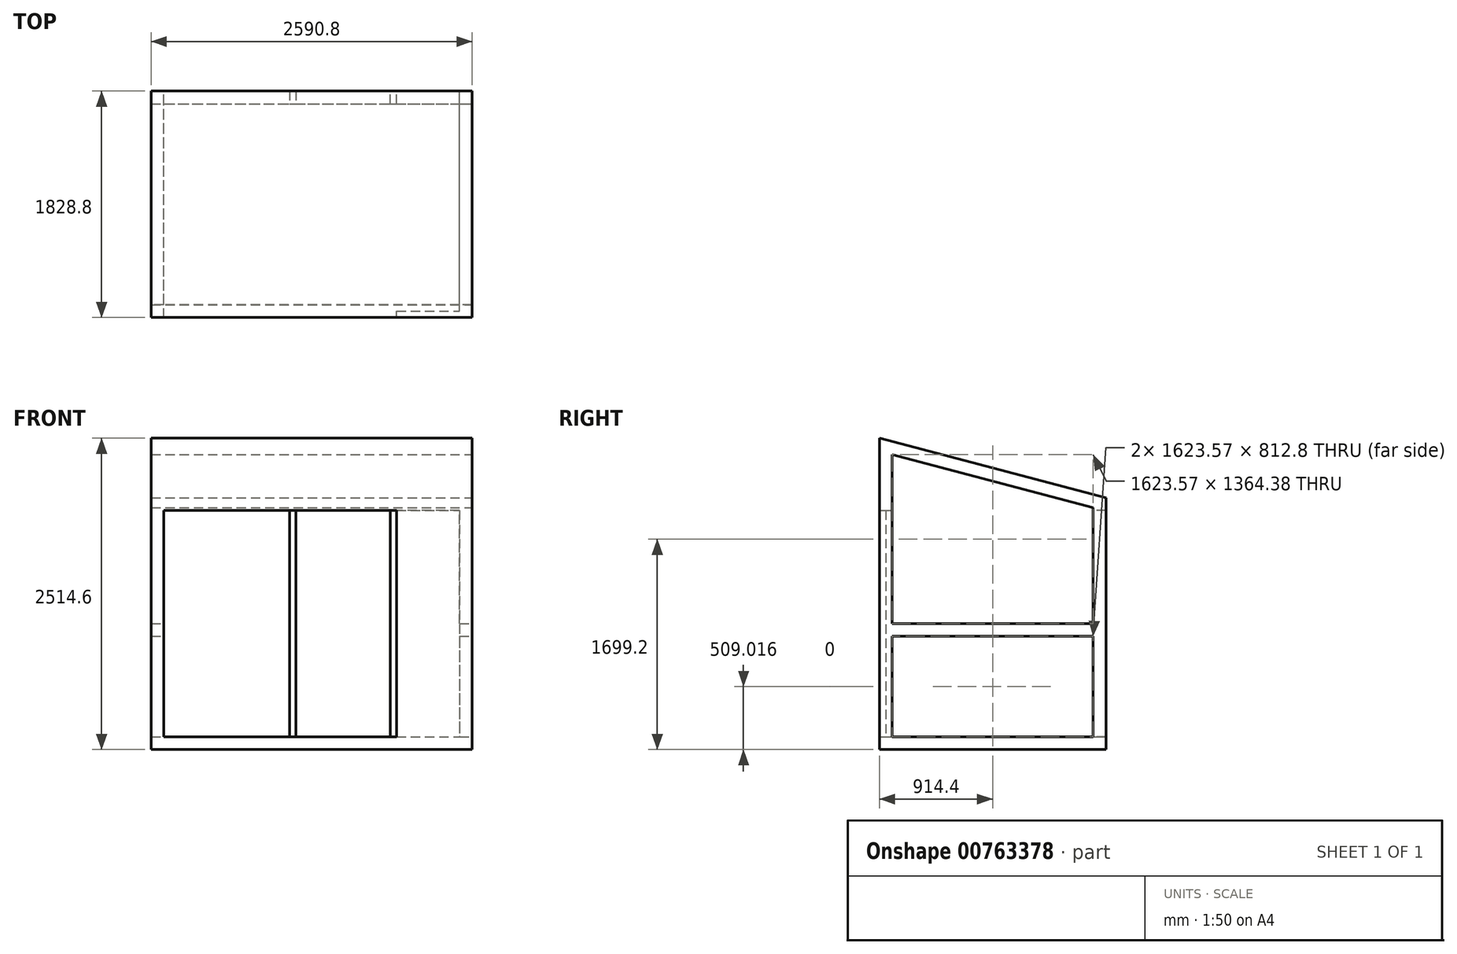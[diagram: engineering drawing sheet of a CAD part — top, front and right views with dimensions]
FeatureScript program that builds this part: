
annotation { "Feature Type Name" : "Feature", "Feature Type Description" : "" }
export const myFeature = defineFeature(function(context is Context, id is Id, definition is map)
    precondition{}
    {
        {
            var Q0;
            Q0=qCreatedBy(makeId("Top.planeOp"),FACE);
            var sketch = newSketch(context, id + "F0", { "sketchPlane" : qUnion([Q0])});
            skLineSegment(sketch, "E0.bottom", {"start": v(-1295.4, 914.4) * mm, "end": v(1295.4, 914.4) * mm});
            skLineSegment(sketch, "E0.top", {"start": v(-1295.4, -914.4) * mm, "end": v(1295.4, -914.4) * mm});
            skLineSegment(sketch, "E0.left", {"start": v(-1295.4, 914.4) * mm, "end": v(-1295.4, -914.4) * mm});
            skLineSegment(sketch, "E0.right", {"start": v(1295.4, 914.4) * mm, "end": v(1295.4, -914.4) * mm});
            skPoint(sketch, "E0.middle", {"position": v(0, 0) * mm});
            skSolve(sketch);
        }
        {
            var Q0;
            Q0=makeQuery(id+"F0.imprint","IMPRINT",FACE,{"disambiguationData":[TD([[makeQuery(id+"F0.imprint","IMPRINT",EDGE,{"derivedFrom":sQuery(id+"F0.wireOp",EDGE,"E0.bottom")}),-1.0]])]});
            extrude(context, id + "F1", {"entities" : qUnion([Q0]), "depth" : 2514.6 * mm, "offsetDistance" : 25.4 * mm});
        }
        {
            var Q0;
            Q0=makeQuery(id+"F1.opExtrude","SWEPT_FACE",FACE,{"disambiguationData":[OSD([sQuery(id+"F0.wireOp",EDGE,"E0.right")])]});
            var sketch = newSketch(context, id + "F2", { "sketchPlane" : qUnion([Q0])});
            skLineSegment(sketch, "E1", {"start": v(-914.4, 2514.6) * mm, "end": v(914.4, 2032) * mm});
            skLineSegment(sketch, "E2", {"start": v(914.4, 2032) * mm, "end": v(914.4, 2514.6) * mm});
            skLineSegment(sketch, "E3", {"start": v(914.4, 2514.6) * mm, "end": v(-914.4, 2514.6) * mm});
            skSolve(sketch);
        }
        {
            var Q0;
            Q0=makeQuery(id+"F2.imprint","IMPRINT",FACE,{"disambiguationData":[TD([[makeQuery(id+"F2.imprint","IMPRINT",EDGE,{"derivedFrom":sQuery(id+"F2.wireOp",EDGE,"E1")}),1.0]])]});
            extrude(context, id + "F3", {"entities" : qUnion([Q0]), "operationType" : NewBodyOperationType.REMOVE, "endBound" : BoundingType.THROUGH_ALL, "oppositeDirection" : true, "depth" : 25.4 * mm, "offsetDistance" : 25.4 * mm});
        }
        {
            var Q0;
            Q0=makeQuery(id+"F1.opExtrude","SWEPT_FACE",FACE,{"disambiguationData":[OSD([sQuery(id+"F0.wireOp",EDGE,"E0.right")])]});
            var sketch = newSketch(context, id + "F4", { "sketchPlane" : qUnion([Q0])});
            skLineSegment(sketch, "E4.0", {"start": v(811.78, 1952.95) * mm, "end": v(-811.78, 2381.4) * mm});
            skLineSegment(sketch, "E4.1", {"start": v(811.78, 102.62) * mm, "end": v(811.78, 1952.95) * mm});
            skLineSegment(sketch, "E4.2", {"start": v(-811.78, 102.62) * mm, "end": v(811.78, 102.62) * mm});
            skLineSegment(sketch, "E4.3", {"start": v(-811.78, 2381.4) * mm, "end": v(-811.78, 102.62) * mm});
            skLineSegment(sketch, "E5.0", {"start": v(812.8, 1953.73) * mm, "end": v(-812.8, 2382.71) * mm});
            skLineSegment(sketch, "E5.1", {"start": v(812.8, 101.6) * mm, "end": v(812.8, 1953.73) * mm});
            skLineSegment(sketch, "E5.2", {"start": v(-812.8, 101.6) * mm, "end": v(812.8, 101.6) * mm});
            skLineSegment(sketch, "E5.3", {"start": v(-812.8, 2382.71) * mm, "end": v(-812.8, 101.6) * mm});
            skSolve(sketch);
        }
        {
            var Q0;
            Q0=makeQuery(id+"F4.imprint","IMPRINT",FACE,{"disambiguationData":[TD([[makeQuery(id+"F4.imprint","IMPRINT",EDGE,{"derivedFrom":sQuery(id+"F4.wireOp",EDGE,"E4.0")}),1.0]])]});
            extrude(context, id + "F5", {"entities" : qUnion([Q0]), "operationType" : NewBodyOperationType.REMOVE, "endBound" : BoundingType.THROUGH_ALL, "oppositeDirection" : true, "depth" : 25.4 * mm, "offsetDistance" : 25.4 * mm});
        }
        {
            var Q0;
            Q0=makeQuery(id+"F1.opExtrude","SWEPT_FACE",FACE,{"disambiguationData":[OSD([sQuery(id+"F0.wireOp",EDGE,"E0.bottom")])]});
            var sketch = newSketch(context, id + "F6", { "sketchPlane" : qUnion([Q0])});
            skLineSegment(sketch, "E6.0", {"start": v(1193.8, 101.6) * mm, "end": v(1193.8, 1930.4) * mm});
            skLineSegment(sketch, "E6.1", {"start": v(-1193.8, 101.6) * mm, "end": v(1193.8, 101.6) * mm});
            skLineSegment(sketch, "E6.2", {"start": v(-1193.8, 1930.4) * mm, "end": v(-1193.8, 101.6) * mm});
            skLineSegment(sketch, "E6.3", {"start": v(1193.8, 1930.4) * mm, "end": v(-1193.8, 1930.4) * mm});
            skSolve(sketch);
        }
        {
            var Q0;
            Q0=makeQuery(id+"F6.imprint","IMPRINT",FACE,{"disambiguationData":[TD([[makeQuery(id+"F6.imprint","IMPRINT",EDGE,{"derivedFrom":sQuery(id+"F6.wireOp",EDGE,"E6.0")}),1.0]])]});
            extrude(context, id + "F7", {"entities" : qUnion([Q0]), "operationType" : NewBodyOperationType.REMOVE, "endBound" : BoundingType.THROUGH_ALL, "oppositeDirection" : true, "depth" : 127 * mm, "offsetDistance" : 25.4 * mm});
        }
        {
            var Q0;
            Q0=makeQuery(id+"F5.boolean.opBoolean","COPY",FACE,{"derivedFrom":makeQuery(id+"F5.opExtrude","SWEPT_FACE",FACE,{"disambiguationData":[OSD([sQuery(id+"F4.wireOp",EDGE,"E4.1")])]})});
            var sketch = newSketch(context, id + "F8", { "sketchPlane" : qUnion([Q0])});
            skLineSegment(sketch, "E7.bottom", {"start": v(-1295.4, 1017.02) * mm, "end": v(-1193.8, 1017.02) * mm});
            skLineSegment(sketch, "E7.top", {"start": v(-1295.4, 915.42) * mm, "end": v(-1193.8, 915.42) * mm});
            skLineSegment(sketch, "E7.left", {"start": v(-1295.4, 1017.02) * mm, "end": v(-1295.4, 915.42) * mm});
            skLineSegment(sketch, "E7.right", {"start": v(-1193.8, 1017.02) * mm, "end": v(-1193.8, 915.42) * mm});
            skLineSegment(sketch, "E8.bottom", {"start": v(1193.8, 915.42) * mm, "end": v(1295.4, 915.42) * mm});
            skLineSegment(sketch, "E8.top", {"start": v(1193.8, 1017.02) * mm, "end": v(1295.4, 1017.02) * mm});
            skLineSegment(sketch, "E8.left", {"start": v(1193.8, 915.42) * mm, "end": v(1193.8, 1017.02) * mm});
            skLineSegment(sketch, "E8.right", {"start": v(1295.4, 915.42) * mm, "end": v(1295.4, 1017.02) * mm});
            skSolve(sketch);
        }
        {
            var Q0;
            Q0 = qSketchRegion(id + "F8", true);
            extrude(context, id + "F9", {"entities" : qUnion([Q0]), "operationType" : NewBodyOperationType.ADD, "depth" : 1625.6 * mm, "offsetDistance" : 25.4 * mm});
        }
        {
            var Q0;
            Q0=makeQuery(id+"F9.boolean.opBoolean","MERGE",FACE,{"derivedFrom":[makeQuery(id+"F7.boolean.opBoolean","COPY",FACE,{"derivedFrom":makeQuery(id+"F7.opExtrude","SWEPT_FACE",FACE,{"disambiguationData":[OSD([sQuery(id+"F6.wireOp",EDGE,"E6.2")])]})}),makeQuery(id+"F9.opExtrude","SWEPT_FACE",FACE,{"disambiguationData":[OSD([sQuery(id+"F8.wireOp",EDGE,"E8.left")])]})]});
            var sketch = newSketch(context, id + "F10", { "sketchPlane" : qUnion([Q0])});
            skLineSegment(sketch, "E9.bottom", {"start": v(914.4, 1930.4) * mm, "end": v(863.6, 1930.4) * mm});
            skLineSegment(sketch, "E9.top", {"start": v(914.4, 101.6) * mm, "end": v(863.6, 101.6) * mm});
            skLineSegment(sketch, "E9.left", {"start": v(914.4, 1930.4) * mm, "end": v(914.4, 101.6) * mm});
            skLineSegment(sketch, "E9.right", {"start": v(863.6, 1930.4) * mm, "end": v(863.6, 101.6) * mm});
            skSolve(sketch);
        }
        {
            var Q0;
            Q0 = qSketchRegion(id + "F10", true);
            extrude(context, id + "F11", {"entities" : qUnion([Q0]), "operationType" : NewBodyOperationType.ADD, "depth" : 508 * mm, "offsetDistance" : 25.4 * mm});
        }
        {
            var Q0;
            Q0=makeQuery(id+"F7.boolean.opBoolean","COPY",FACE,{"disambiguationData":[TD([makeQuery(id+"F1.opExtrude","SWEPT_FACE",FACE,{"disambiguationData":[OSD([sQuery(id+"F0.wireOp",EDGE,"E0.bottom")])]})])],"derivedFrom":makeQuery(id+"F7.opExtrude","SWEPT_FACE",FACE,{"disambiguationData":[OSD([sQuery(id+"F6.wireOp",EDGE,"E6.3")])]})});
            var sketch = newSketch(context, id + "F12", { "sketchPlane" : qUnion([Q0])});
            skLineSegment(sketch, "E10.bottom", {"start": v(685.8, -811.78) * mm, "end": v(635, -811.78) * mm});
            skLineSegment(sketch, "E10.top", {"start": v(685.8, -914.4) * mm, "end": v(635, -914.4) * mm});
            skLineSegment(sketch, "E10.left", {"start": v(685.8, -811.78) * mm, "end": v(685.8, -914.4) * mm});
            skLineSegment(sketch, "E10.right", {"start": v(635, -811.78) * mm, "end": v(635, -914.4) * mm});
            skLineSegment(sketch, "E11.bottom", {"start": v(-177.8, -914.4) * mm, "end": v(-127, -914.4) * mm});
            skLineSegment(sketch, "E11.top", {"start": v(-177.8, -811.78) * mm, "end": v(-127, -811.78) * mm});
            skLineSegment(sketch, "E11.left", {"start": v(-177.8, -914.4) * mm, "end": v(-177.8, -811.78) * mm});
            skLineSegment(sketch, "E11.right", {"start": v(-127, -914.4) * mm, "end": v(-127, -811.78) * mm});
            skSolve(sketch);
        }
        {
            var Q0;
            Q0 = qSketchRegion(id + "F12", true);
            extrude(context, id + "F13", {"entities" : qUnion([Q0]), "operationType" : NewBodyOperationType.ADD, "depth" : 1828.8 * mm, "offsetDistance" : 25.4 * mm});
        }
    });
